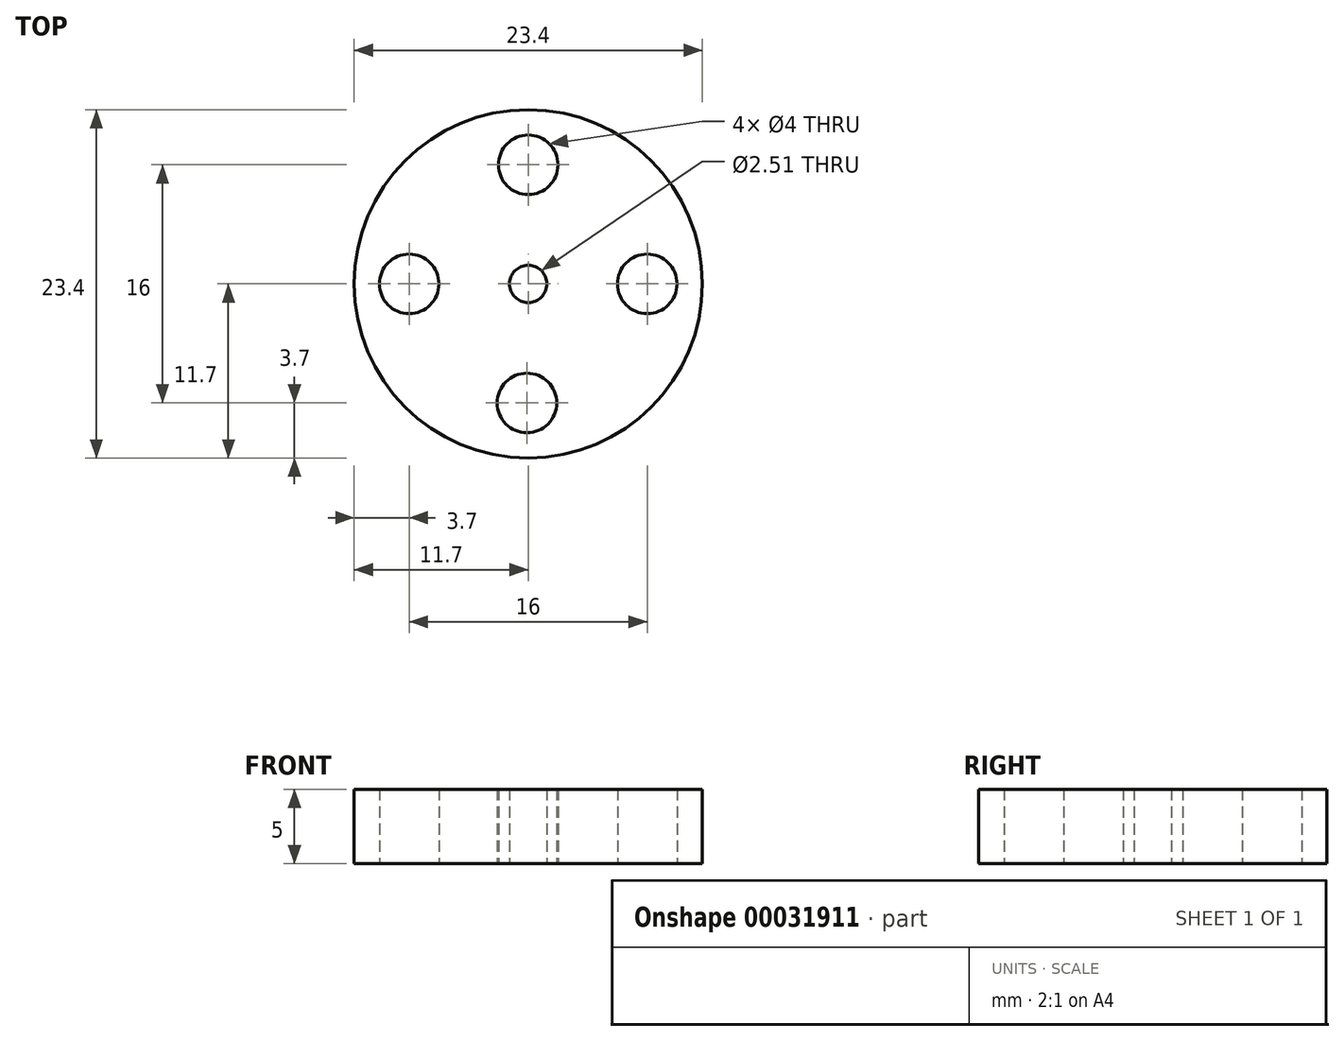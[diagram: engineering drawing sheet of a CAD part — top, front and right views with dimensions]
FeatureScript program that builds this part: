
annotation { "Feature Type Name" : "Feature", "Feature Type Description" : "" }
export const myFeature = defineFeature(function(context is Context, id is Id, definition is map)
    precondition{}
    {
        {
            var Q0;
            Q0=qCreatedBy(makeId("Top.planeOp"),FACE);
            var sketch = newSketch(context, id + "F0", { "sketchPlane" : qUnion([Q0])});
            skCircle(sketch, "E0", {"center": v(0, 0) * mm, "radius": 11.7 * mm});
            skCircle(sketch, "E1", {"center": v(0, 8) * mm, "radius": 2 * mm});
            skCircle(sketch, "E2", {"center": v(-0.08, -8) * mm, "radius": 2 * mm});
            skCircle(sketch, "E3", {"center": v(8, 0) * mm, "radius": 2 * mm});
            skCircle(sketch, "E4", {"center": v(-8, 0) * mm, "radius": 2 * mm});
            skCircle(sketch, "E5", {"center": v(0, 0) * mm, "radius": 1.25 * mm});
            skSolve(sketch);
        }
        {
            var Q0;
            Q0=makeQuery(id+"F0.imprint","IMPRINT",FACE,{"disambiguationData":[TD([[makeQuery(id+"F0.imprint","IMPRINT",EDGE,{"derivedFrom":sQuery(id+"F0.wireOp",EDGE,"E0")}),1.0]])]});
            var Q1;
            Q1=sQuery(id+"F0.wireOp",EDGE,"E0");
            var Q2;
            Q2=sQuery(id+"F0.wireOp",EDGE,"E1");
            var Q3;
            Q3=sQuery(id+"F0.wireOp",EDGE,"E2");
            var Q4;
            Q4=sQuery(id+"F0.wireOp",EDGE,"E3");
            var Q5;
            Q5=sQuery(id+"F0.wireOp",EDGE,"E4");
            var Q6;
            Q6=sQuery(id+"F0.wireOp",EDGE,"E5");
            extrude(context, id + "F1", {"entities" : qUnion([Q0]), "surfaceEntities" : qUnion([Q1, Q2, Q3, Q4, Q5, Q6]), "depth" : 5 * mm});
        }
    });
